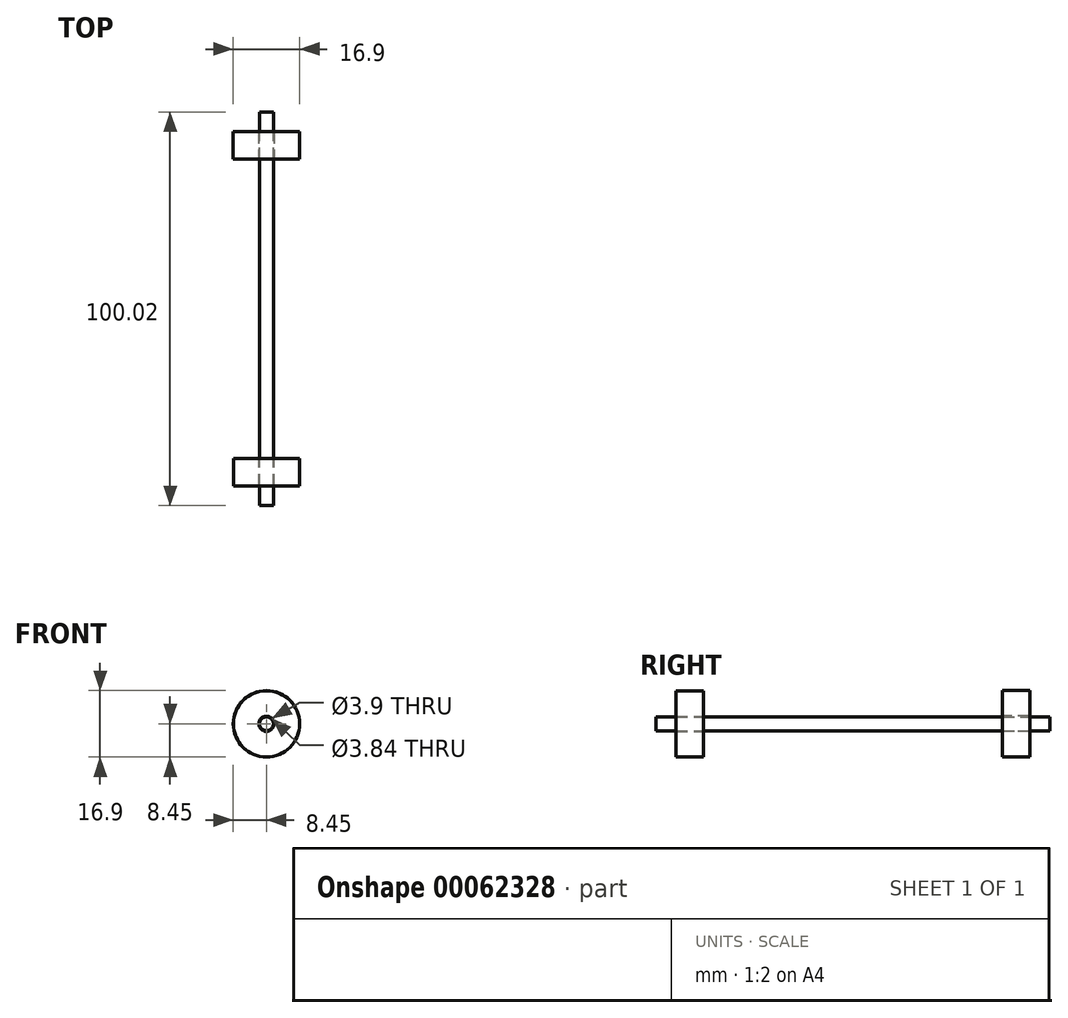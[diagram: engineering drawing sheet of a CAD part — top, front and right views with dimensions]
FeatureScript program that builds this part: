
annotation { "Feature Type Name" : "Feature", "Feature Type Description" : "" }
export const myFeature = defineFeature(function(context is Context, id is Id, definition is map)
    precondition{}
    {
        {
            var Q0;
            Q0=qCreatedBy(makeId("Front.planeOp"),FACE);
            cPlane(context, id + "F0", {"entities" : qUnion([Q0]), "cplaneType" : CPlaneType.OFFSET, "offset" : 38 * mm, "width" : 152.4 * mm, "height" : 152.4 * mm});
        }
        {
            var Q0;
            Q0=qCreatedBy(makeId("Front.planeOp"),FACE);
            cPlane(context, id + "F1", {"entities" : qUnion([Q0]), "cplaneType" : CPlaneType.OFFSET, "offset" : 38 * mm, "oppositeDirection" : true, "width" : 152.4 * mm, "height" : 152.4 * mm});
        }
        {
            var Q0;
            Q0=qCreatedBy(id+"F0.planeOp",FACE);
            var sketch = newSketch(context, id + "F2", { "sketchPlane" : qUnion([Q0])});
            skCircle(sketch, "E0", {"center": v(0, 0) * mm, "radius": 8.4 * mm});
            skSolve(sketch);
        }
        {
            var Q0;
            Q0=qCreatedBy(id+"F0.planeOp",FACE);
            var sketch = newSketch(context, id + "F3", { "sketchPlane" : qUnion([Q0])});
            skCircle(sketch, "E1", {"center": v(0, 0) * mm, "radius": 1.92 * mm});
            skSolve(sketch);
        }
        {
            var Q0;
            Q0 = qSketchRegion(id + "F2", true);
            extrude(context, id + "F4", {"entities" : qUnion([Q0]), "depth" : 7 * mm});
        }
        {
            var Q0;
            Q0=makeQuery(id+"F3.imprint","IMPRINT",FACE,{"disambiguationData":[TD([[makeQuery(id+"F3.imprint","IMPRINT",EDGE,{"derivedFrom":sQuery(id+"F3.wireOp",EDGE,"E1")}),1.0]])]});
            extrude(context, id + "F5", {"entities" : qUnion([Q0]), "operationType" : NewBodyOperationType.REMOVE, "depth" : 7.58 * mm});
        }
        {
            var Q0;
            Q0=qCreatedBy(makeId("Front.planeOp"),FACE);
            var sketch = newSketch(context, id + "F6", { "sketchPlane" : qUnion([Q0])});
            skCircle(sketch, "E2", {"center": v(0, 0) * mm, "radius": 1.75 * mm});
            skSolve(sketch);
        }
        {
            var Q0;
            Q0=makeQuery(id+"F6.imprint","IMPRINT",FACE,{"disambiguationData":[TD([[makeQuery(id+"F6.imprint","IMPRINT",EDGE,{"derivedFrom":sQuery(id+"F6.wireOp",EDGE,"E2")}),1.0]])]});
            var Q1;
            Q1 = qSketchRegion(id + "F8", true);
            extrude(context, id + "F7", {"entities" : qUnion([Q0, Q1]), "depth" : 50 * mm});
        }
        {
            var Q0;
            Q0=qCreatedBy(id+"F1.planeOp",FACE);
            var sketch = newSketch(context, id + "F8", { "sketchPlane" : qUnion([Q0])});
            skCircle(sketch, "E3", {"center": v(0, 0) * mm, "radius": 8.45 * mm});
            skSolve(sketch);
        }
        {
            var Q0;
            Q0=qCreatedBy(id+"F1.planeOp",FACE);
            var sketch = newSketch(context, id + "F9", { "sketchPlane" : qUnion([Q0])});
            skCircle(sketch, "E4", {"center": v(0, 0) * mm, "radius": 1.95 * mm});
            skSolve(sketch);
        }
        {
            var Q0;
            Q0 = qSketchRegion(id + "F8", true);
            extrude(context, id + "F10", {"entities" : qUnion([Q0]), "oppositeDirection" : true, "depth" : 7 * mm});
        }
        {
            var Q0;
            Q0 = qSketchRegion(id + "F9", true);
            extrude(context, id + "F11", {"entities" : qUnion([Q0]), "operationType" : NewBodyOperationType.REMOVE, "oppositeDirection" : true, "depth" : 10.06 * mm});
        }
        {
            var Q0;
            Q0 = qSketchRegion(id + "F6", true);
            extrude(context, id + "F12", {"entities" : qUnion([Q0]), "operationType" : NewBodyOperationType.ADD, "oppositeDirection" : true, "depth" : 50 * mm});
        }
    });
